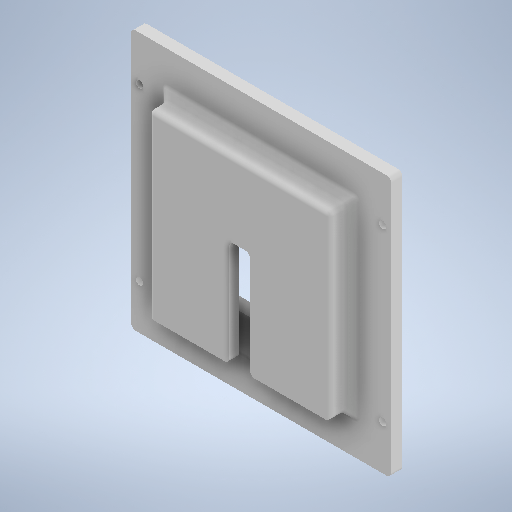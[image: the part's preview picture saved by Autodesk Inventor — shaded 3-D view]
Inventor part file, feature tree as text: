
AUTODESK INVENTOR PART (.ipt)
format: ipt  version: 2025.1 (Build 291241000, 241)  size: 430,592 bytes
history: native  units: mm
features: sketch x5, extrude x5, fillet x5, chamfer x2
ambient origin geometry x8: Origin, YZ Plane, XZ Plane, XY Plane, X Axis, Y Axis, Z Axis, Center Point
bodies: Body1 (feature_tree)
feature tree (17):
  sketch  "Sketch3"  dims[d5=3.2mm d16=75.4mm]
  extrude  "Extrusion3"  Depth=3.2mm
  extrude  "Extrusion4"  Depth=75.4mm
  extrude  "Extrusion5"  Depth=3.2mm
  extrude  "Extrusion6"  Depth=5.0mm TaperAngle=0.0deg
  extrude  "Extrusion7"  Depth=2.0mm
  chamfer  "Chamfer1"  Distance=50.0mm
  fillet  "Fillet1"  Radius=50.0mm
  chamfer  "Chamfer2"  Distance=5.0mm
  fillet  "Fillet2"  Radius=5.0mm
  fillet  "Fillet3"  Radius=4.5mm
  fillet  "Fillet4"  Radius=9.2mm
  fillet  "Fillet5"  Radius=9.2mm
  sketch  "Sketch1"  dims[d1=115.0mm d4=3.2mm]
  sketch  "Sketch4"  dims[d20=3.2mm d23=3.2mm]
  sketch  "Sketch5"  dims[d24=115.0mm d40=5.0mm d41=0.0mm]
  sketch  "Sketch6"  dims[d42=80.0mm d43=80.0mm d44=50.0mm d45=50.0mm d46=5.0mm d47=0.0mm d48=5.0mm d49=0.0mm d50=4.5mm d51=0.0mm d55=9.2mm d56=9.2mm d57=4.5mm d58=0.0mm d59=40.0mm d60=40.0mm d61=47.0mm d62=18.0mm d63=9.2mm d65=9.0mm d66=9.0mm d67=4.6mm d68=3.0mm d69=16.0mm d70=0.0mm d71=3.0mm d72=2.0mm d73=45.0deg d74=2.0mm d75=2.0mm d76=2.0mm d77=45.0deg d78=2.0mm d79=2.0mm d80=2.0mm d81=2.0mm d84=107.5mm d85=75.4mm d86=19.8mm d87=19.8mm d88=19.8mm d89=19.8mm d90=107.5mm d91=78.6mm d92=18.2mm]
